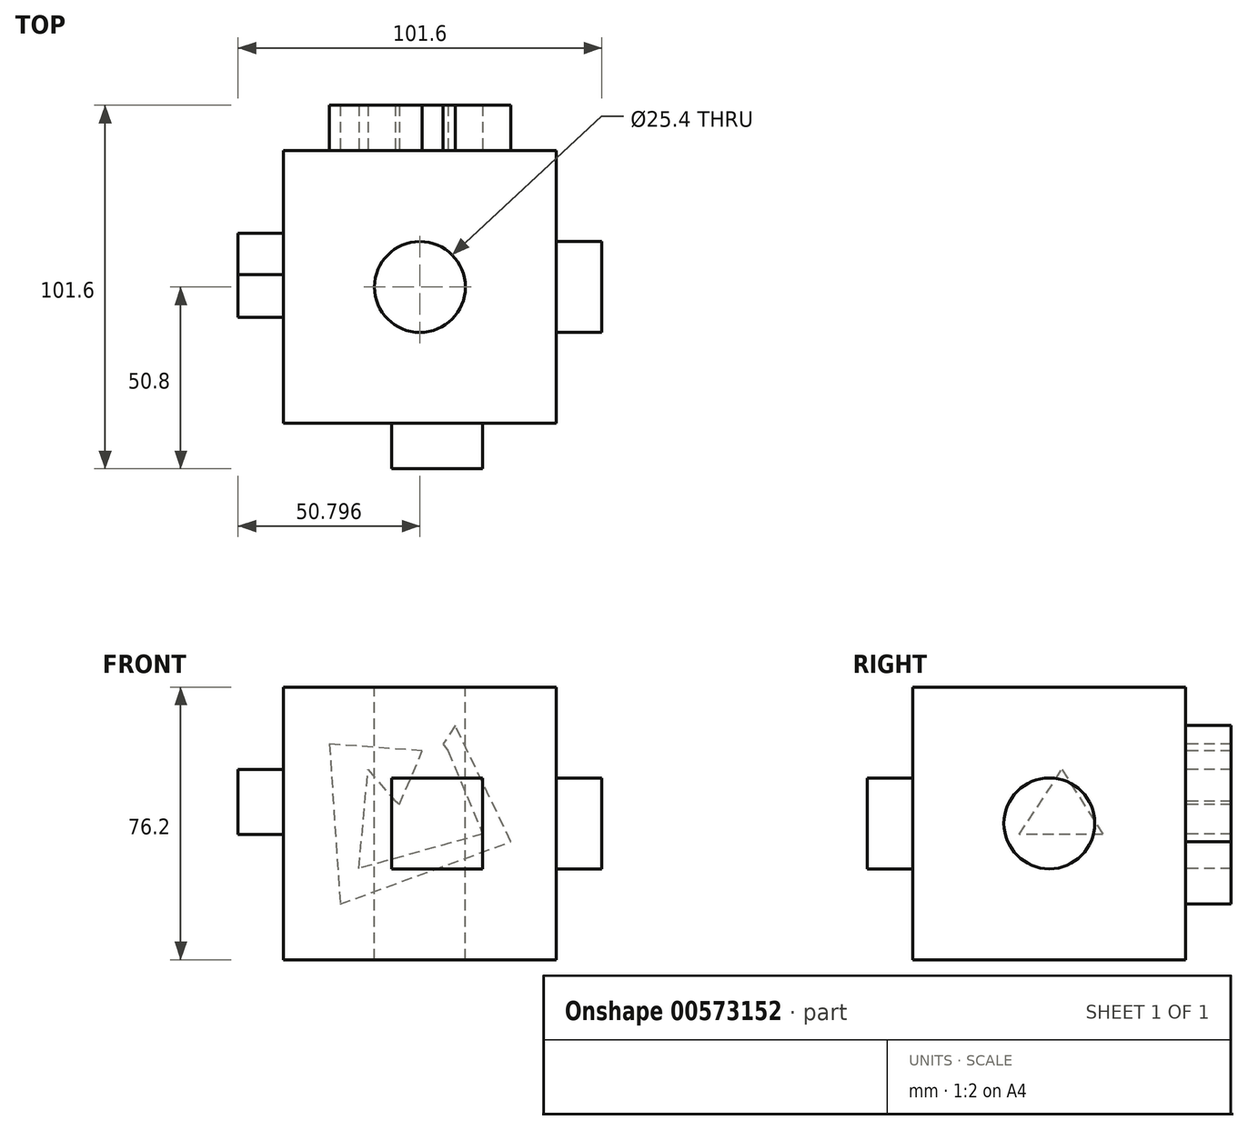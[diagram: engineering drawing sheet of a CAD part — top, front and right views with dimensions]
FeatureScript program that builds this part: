
annotation { "Feature Type Name" : "Feature", "Feature Type Description" : "" }
export const myFeature = defineFeature(function(context is Context, id is Id, definition is map)
    precondition{}
    {
        {
            var Q0;
            Q0=qCreatedBy(makeId("Front.planeOp"),FACE);
            var sketch = newSketch(context, id + "F0", { "sketchPlane" : qUnion([Q0])});
            skLineSegment(sketch, "E0.bottom", {"start": v(-55.65, 75.52) * mm, "end": v(20.55, 75.52) * mm});
            skLineSegment(sketch, "E0.top", {"start": v(-55.65, -0.68) * mm, "end": v(20.55, -0.68) * mm});
            skLineSegment(sketch, "E0.left", {"start": v(-55.65, 75.52) * mm, "end": v(-55.65, -0.68) * mm});
            skLineSegment(sketch, "E0.right", {"start": v(20.55, 75.52) * mm, "end": v(20.55, -0.68) * mm});
            skSolve(sketch);
        }
        {
            var Q0;
            Q0=makeQuery(id+"F0.imprint","IMPRINT",FACE,{"disambiguationData":[TD([[makeQuery(id+"F0.imprint","IMPRINT",EDGE,{"derivedFrom":sQuery(id+"F0.wireOp",EDGE,"E0.bottom")}),-1.0]])]});
            extrude(context, id + "F1", {"entities" : qUnion([Q0]), "depth" : 76.2 * mm, "offsetDistance" : 25.4 * mm});
        }
        {
            var Q0;
            Q0=makeQuery(id+"F1.opExtrude","CAP_FACE",FACE,{"disambiguationData":[OSD([sQuery(id+"F0.wireOp",EDGE,"E0.bottom"),sQuery(id+"F0.wireOp",EDGE,"E0.top"),sQuery(id+"F0.wireOp",EDGE,"E0.left"),sQuery(id+"F0.wireOp",EDGE,"E0.right")])],"isStart":false});
            var sketch = newSketch(context, id + "F2", { "sketchPlane" : qUnion([Q0])});
            skLineSegment(sketch, "E1.bottom", {"start": v(-25.4, 50.12) * mm, "end": v(0, 50.12) * mm});
            skLineSegment(sketch, "E1.top", {"start": v(-25.4, 24.72) * mm, "end": v(0, 24.72) * mm});
            skLineSegment(sketch, "E1.left", {"start": v(-25.4, 50.12) * mm, "end": v(-25.4, 24.72) * mm});
            skLineSegment(sketch, "E1.right", {"start": v(0, 50.12) * mm, "end": v(0, 24.72) * mm});
            skSolve(sketch);
        }
        {
            var Q0;
            Q0=makeQuery(id+"F2.imprint","IMPRINT",FACE,{"disambiguationData":[TD([[makeQuery(id+"F2.imprint","IMPRINT",EDGE,{"derivedFrom":sQuery(id+"F2.wireOp",EDGE,"E1.bottom")}),-1.0]])]});
            extrude(context, id + "F3", {"entities" : qUnion([Q0]), "operationType" : NewBodyOperationType.ADD, "depth" : 12.7 * mm, "offsetDistance" : 25.4 * mm});
        }
        {
            var Q0;
            Q0=makeQuery(id+"F1.opExtrude","SWEPT_FACE",FACE,{"disambiguationData":[OSD([sQuery(id+"F0.wireOp",EDGE,"E0.right")])]});
            var sketch = newSketch(context, id + "F4", { "sketchPlane" : qUnion([Q0])});
            skCircle(sketch, "E2", {"center": v(-38.1, 37.42) * mm, "radius": 12.7 * mm});
            skPoint(sketch, "E2.centerSnap0", {"position": v(0, 37.42) * mm});
            skSolve(sketch);
        }
        {
            var Q0;
            Q0=makeQuery(id+"F4.imprint","IMPRINT",FACE,{"disambiguationData":[TD([[makeQuery(id+"F4.imprint","IMPRINT",EDGE,{"derivedFrom":sQuery(id+"F4.wireOp",EDGE,"E2")}),1.0]])]});
            extrude(context, id + "F5", {"entities" : qUnion([Q0]), "operationType" : NewBodyOperationType.ADD, "depth" : 12.7 * mm, "offsetDistance" : 25.4 * mm});
        }
        {
            var Q0;
            Q0=makeQuery(id+"F1.opExtrude","SWEPT_FACE",FACE,{"disambiguationData":[OSD([sQuery(id+"F0.wireOp",EDGE,"E0.bottom")])]});
            var sketch = newSketch(context, id + "F6", { "sketchPlane" : qUnion([Q0])});
            skPoint(sketch, "E3", {"position": v(-17.55, -38.1) * mm});
            skPoint(sketch, "E3.positionSnap0", {"position": v(-55.65, -38.1) * mm});
            skSolve(sketch);
        }
        {
            var Q0;
            Q0=sQuery(id+"F6.wireOp",VERTEX,"E3");
            var Q1;
            Q1=makeQuery(id+"F1.opExtrude","SWEPT_BODY",BODY,{"disambiguationData":[OSD([sQuery(id+"F0.wireOp",EDGE,"E0.bottom"),sQuery(id+"F0.wireOp",EDGE,"E0.top"),sQuery(id+"F0.wireOp",EDGE,"E0.left"),sQuery(id+"F0.wireOp",EDGE,"E0.right")])]});
            hole(context, id + "F7", {"style" : HoleStyle.SIMPLE, "endStyle" : HoleEndStyle.THROUGH, "holeDiameter" : 25.4 * mm, "isTappedThrough" : true, "tappedDepth" : 12.7 * mm, "tapClearance" : 3, "locations" : qUnion([Q0]), "scope" : qUnion([Q1])});
        }
        {
            var Q0;
            Q0=makeQuery(id+"F1.opExtrude","SWEPT_FACE",FACE,{"disambiguationData":[OSD([sQuery(id+"F0.wireOp",EDGE,"E0.left")])]});
            var sketch = newSketch(context, id + "F8", { "sketchPlane" : qUnion([Q0])});
            skLineSegment(sketch, "E4", {"start": v(34.6, 52.5) * mm, "end": v(23.12, 34.3) * mm});
            skLineSegment(sketch, "E5", {"start": v(23.12, 34.3) * mm, "end": v(46.54, 34.3) * mm});
            skLineSegment(sketch, "E6", {"start": v(46.54, 34.3) * mm, "end": v(34.6, 52.5) * mm});
            skSolve(sketch);
        }
        {
            var Q0;
            Q0=makeQuery(id+"F8.imprint","IMPRINT",FACE,{"disambiguationData":[TD([[makeQuery(id+"F8.imprint","IMPRINT",EDGE,{"derivedFrom":sQuery(id+"F8.wireOp",EDGE,"E4")}),1.0]])]});
            extrude(context, id + "F9", {"entities" : qUnion([Q0]), "operationType" : NewBodyOperationType.ADD, "depth" : 12.7 * mm, "offsetDistance" : 25.4 * mm});
        }
        {
            var Q0;
            Q0=makeQuery(id+"F1.opExtrude","CAP_FACE",FACE,{"disambiguationData":[OSD([sQuery(id+"F0.wireOp",EDGE,"E0.bottom"),sQuery(id+"F0.wireOp",EDGE,"E0.top"),sQuery(id+"F0.wireOp",EDGE,"E0.left"),sQuery(id+"F0.wireOp",EDGE,"E0.right")])],"isStart":true});
            var sketch = newSketch(context, id + "F10", { "sketchPlane" : qUnion([Q0])});
            skLineSegment(sketch, "E7", {"start": v(11.1, 59.57) * mm, "end": v(9.67, 57.69) * mm});
            skLineSegment(sketch, "E8", {"start": v(9.67, 57.69) * mm, "end": v(0, 34.45) * mm});
            skLineSegment(sketch, "E9", {"start": v(0, 34.45) * mm, "end": v(34.6, 24.82) * mm});
            skLineSegment(sketch, "E10", {"start": v(34.6, 24.82) * mm, "end": v(32.06, 52.44) * mm});
            skLineSegment(sketch, "E11", {"start": v(32.06, 52.44) * mm, "end": v(24.47, 43.57) * mm});
            skLineSegment(sketch, "E12", {"start": v(23.26, 42.7) * mm, "end": v(24.47, 43.57) * mm});
            skLineSegment(sketch, "E13", {"start": v(23.26, 42.7) * mm, "end": v(16.9, 57.69) * mm});
            skLineSegment(sketch, "E14", {"start": v(16.9, 57.69) * mm, "end": v(42.82, 59.57) * mm});
            skLineSegment(sketch, "E15", {"start": v(42.82, 59.57) * mm, "end": v(39.84, 14.85) * mm});
            skLineSegment(sketch, "E16", {"start": v(39.84, 14.85) * mm, "end": v(-7.84, 32.31) * mm});
            skLineSegment(sketch, "E17", {"start": v(-7.84, 32.31) * mm, "end": v(7.69, 64.75) * mm});
            skLineSegment(sketch, "E18", {"start": v(7.69, 64.75) * mm, "end": v(11.1, 59.57) * mm});
            skSolve(sketch);
        }
        {
            var Q0;
            Q0=makeQuery(id+"F10.imprint","IMPRINT",FACE,{"disambiguationData":[TD([[makeQuery(id+"F10.imprint","IMPRINT",EDGE,{"derivedFrom":sQuery(id+"F10.wireOp",EDGE,"E7")}),-1.0]])]});
            extrude(context, id + "F11", {"entities" : qUnion([Q0]), "operationType" : NewBodyOperationType.ADD, "depth" : 12.7 * mm, "offsetDistance" : 25.4 * mm});
        }
    });
